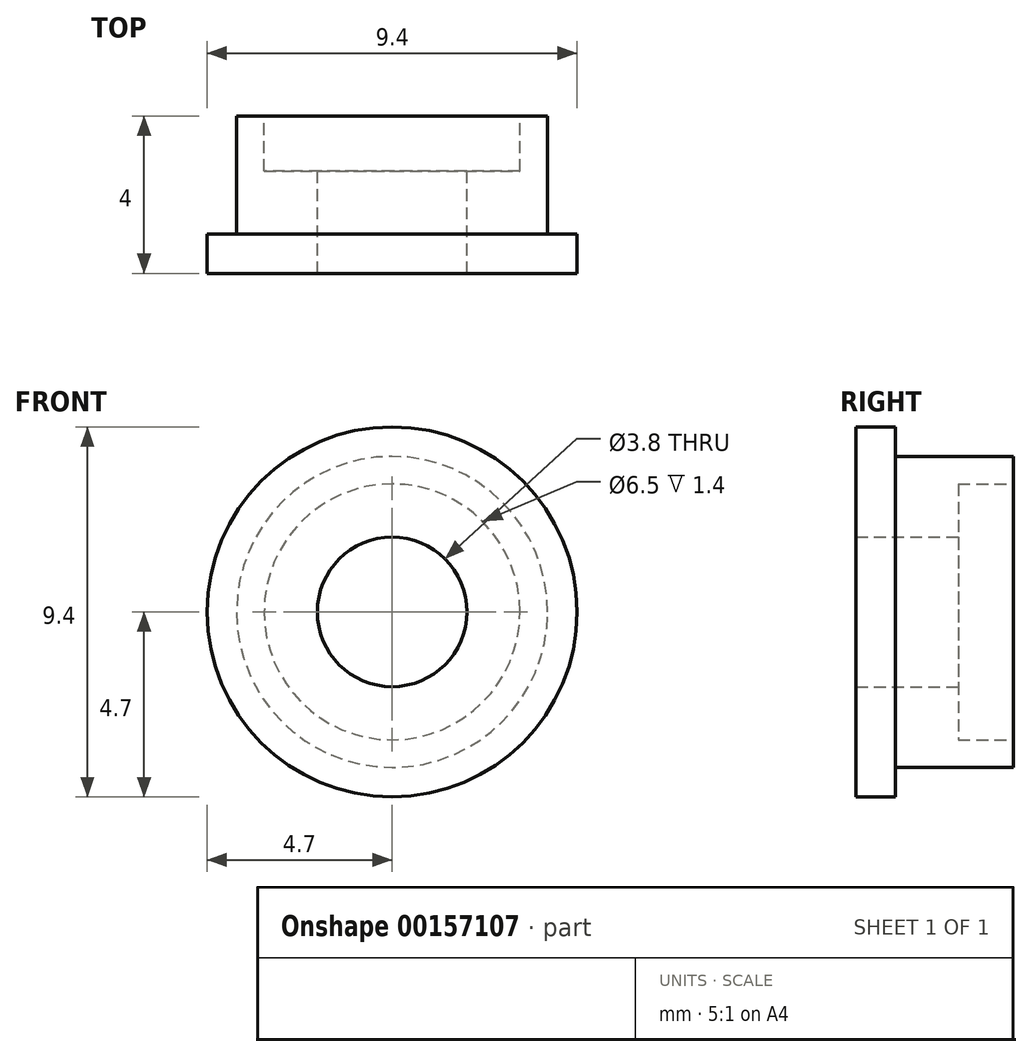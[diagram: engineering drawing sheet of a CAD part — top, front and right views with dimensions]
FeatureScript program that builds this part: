
annotation { "Feature Type Name" : "Feature", "Feature Type Description" : "" }
export const myFeature = defineFeature(function(context is Context, id is Id, definition is map)
    precondition{}
    {
        {
            var Q0;
            Q0=qCreatedBy(makeId("Right.planeOp"),FACE);
            var sketch = newSketch(context, id + "F0", { "sketchPlane" : qUnion([Q0])});
            skLineSegment(sketch, "E0", {"start": v(11.47, 0) * mm, "end": v(0, 0) * mm, "construction": true});
            skLineSegment(sketch, "E1", {"start": v(2.6, 1.9) * mm, "end": v(0, 1.9) * mm});
            skLineSegment(sketch, "E2", {"start": v(2.6, 1.9) * mm, "end": v(2.6, 3.25) * mm});
            skLineSegment(sketch, "E3", {"start": v(4, 3.25) * mm, "end": v(2.6, 3.25) * mm});
            skLineSegment(sketch, "E4", {"start": v(4, 3.25) * mm, "end": v(4, 3.95) * mm});
            skLineSegment(sketch, "E5", {"start": v(1, 3.95) * mm, "end": v(4, 3.95) * mm});
            skLineSegment(sketch, "E6", {"start": v(1, 3.95) * mm, "end": v(1, 4.7) * mm});
            skLineSegment(sketch, "E7", {"start": v(0, 4.7) * mm, "end": v(1, 4.7) * mm});
            skLineSegment(sketch, "E8", {"start": v(0, 4.7) * mm, "end": v(0, 1.9) * mm});
            skSolve(sketch);
        }
        {
            var Q0;
            Q0=makeQuery(id+"F0.imprint","IMPRINT",FACE,{"disambiguationData":[TD([[makeQuery(id+"F0.imprint","IMPRINT",EDGE,{"derivedFrom":sQuery(id+"F0.wireOp",EDGE,"E1")}),-1.0]])]});
            var Q1;
            Q1=sQuery(id+"F0.wireOp",EDGE,"E0");
            revolve(context, id + "F1", {"entities" : qUnion([Q0]), "axis" : qUnion([Q1]), "revolveType" : RevolveType.FULL});
        }
    });
